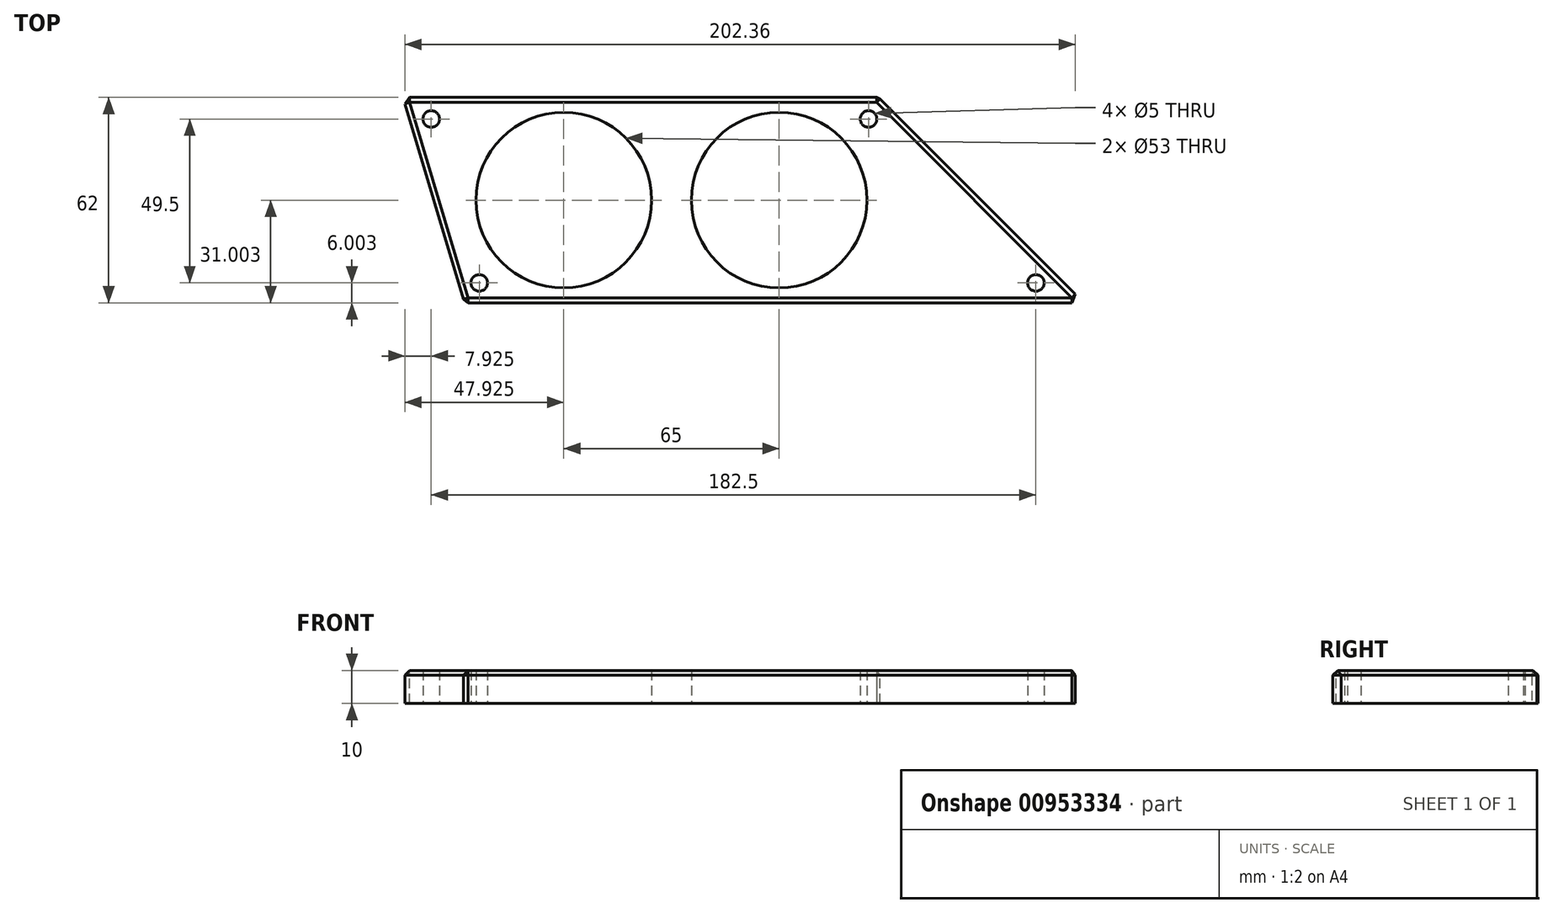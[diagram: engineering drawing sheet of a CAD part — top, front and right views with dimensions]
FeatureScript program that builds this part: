
annotation { "Feature Type Name" : "Feature", "Feature Type Description" : "" }
export const myFeature = defineFeature(function(context is Context, id is Id, definition is map)
    precondition{}
    {
        {
            var Q0;
            Q0=qCreatedBy(makeId("Top.planeOp"),FACE);
            var sketch = newSketch(context, id + "F0", { "sketchPlane" : qUnion([Q0])});
            skLineSegment(sketch, "E0", {"start": v(-45.67, 49.77) * mm, "end": v(97.83, 49.77) * mm});
            skLineSegment(sketch, "E1", {"start": v(97.83, 49.77) * mm, "end": v(159.83, -12.23) * mm});
            skLineSegment(sketch, "E2", {"start": v(159.83, -12.23) * mm, "end": v(-27.17, -12.23) * mm});
            skLineSegment(sketch, "E3", {"start": v(-27.17, -12.23) * mm, "end": v(-45.67, 49.77) * mm});
            skCircle(sketch, "E4", {"center": v(2.83, 18.77) * mm, "radius": 26.5 * mm});
            skCircle(sketch, "E5", {"center": v(67.83, 18.77) * mm, "radius": 26.5 * mm});
            skPoint(sketch, "E6", {"position": v(-37.17, 43.27) * mm});
            skPoint(sketch, "E7", {"position": v(-22.67, -6.23) * mm});
            skPoint(sketch, "E8", {"position": v(94.83, 43.27) * mm});
            skPoint(sketch, "E9", {"position": v(145.33, -6.23) * mm});
            skSolve(sketch);
        }
        {
            var Q0;
            Q0=makeQuery(id+"F0.imprint","IMPRINT",FACE,{"disambiguationData":[TD([[makeQuery(id+"F0.imprint","IMPRINT",EDGE,{"derivedFrom":sQuery(id+"F0.wireOp",EDGE,"E0")}),-1.0]])]});
            extrude(context, id + "F1", {"entities" : qUnion([Q0]), "depth" : 10 * mm, "offsetDistance" : 25 * mm});
        }
        {
            var Q0;
            Q0=sQuery(id+"F0.wireOp",VERTEX,"E6");
            var Q1;
            Q1=sQuery(id+"F0.wireOp",VERTEX,"E7");
            var Q2;
            Q2=sQuery(id+"F0.wireOp",VERTEX,"E8");
            var Q3;
            Q3=sQuery(id+"F0.wireOp",VERTEX,"E9");
            var Q4;
            Q4=makeQuery(id+"F1.opExtrude","SWEPT_BODY",BODY,{"disambiguationData":[OSD([sQuery(id+"F0.wireOp",EDGE,"E0"),sQuery(id+"F0.wireOp",EDGE,"E1"),sQuery(id+"F0.wireOp",EDGE,"E2"),sQuery(id+"F0.wireOp",EDGE,"E3"),sQuery(id+"F0.wireOp",EDGE,"E4"),sQuery(id+"F0.wireOp",EDGE,"E5")])]});
            hole(context, id + "F2", {"style" : HoleStyle.SIMPLE, "endStyle" : HoleEndStyle.BLIND, "oppositeDirection" : true, "holeDiameter" : 5 * mm, "majorDiameter" : 5 * mm, "holeDepth" : 25 * mm, "isTappedThrough" : true, "tappedDepth" : 5 * mm, "tapClearance" : 3, "startFromSketch" : true, "locations" : qUnion([Q0, Q1, Q2, Q3]), "scope" : qUnion([Q4])});
        }
        {
            var Q0;
            Q0=makeQuery(id+"F2.hole-0.boolean.opBoolean","INTERSECT",EDGE,{"derivedFrom":[makeQuery(id+"F1.opExtrude","CAP_FACE",FACE,{"disambiguationData":[OSD([sQuery(id+"F0.wireOp",EDGE,"E0"),sQuery(id+"F0.wireOp",EDGE,"E1"),sQuery(id+"F0.wireOp",EDGE,"E2"),sQuery(id+"F0.wireOp",EDGE,"E3"),sQuery(id+"F0.wireOp",EDGE,"E4"),sQuery(id+"F0.wireOp",EDGE,"E5")])],"isStart":false}),makeQuery(id+"F2.hole-0.opRevolve","SWEPT_FACE",FACE,{"disambiguationData":[OSD([sQuery(id+"F2.hole-0.sketch.wireOp",EDGE,"core_line_2")])]})]});
            var Q1;
            Q1=makeQuery(id+"F2.hole-1.boolean.opBoolean","INTERSECT",EDGE,{"derivedFrom":[makeQuery(id+"F1.opExtrude","CAP_FACE",FACE,{"disambiguationData":[OSD([sQuery(id+"F0.wireOp",EDGE,"E0"),sQuery(id+"F0.wireOp",EDGE,"E1"),sQuery(id+"F0.wireOp",EDGE,"E2"),sQuery(id+"F0.wireOp",EDGE,"E3"),sQuery(id+"F0.wireOp",EDGE,"E4"),sQuery(id+"F0.wireOp",EDGE,"E5")])],"isStart":false}),makeQuery(id+"F2.hole-1.opRevolve","SWEPT_FACE",FACE,{"disambiguationData":[OSD([sQuery(id+"F2.hole-1.sketch.wireOp",EDGE,"core_line_2")])]})]});
            var Q2;
            Q2=makeQuery(id+"F2.hole-2.boolean.opBoolean","INTERSECT",EDGE,{"derivedFrom":[makeQuery(id+"F1.opExtrude","CAP_FACE",FACE,{"disambiguationData":[OSD([sQuery(id+"F0.wireOp",EDGE,"E0"),sQuery(id+"F0.wireOp",EDGE,"E1"),sQuery(id+"F0.wireOp",EDGE,"E2"),sQuery(id+"F0.wireOp",EDGE,"E3"),sQuery(id+"F0.wireOp",EDGE,"E4"),sQuery(id+"F0.wireOp",EDGE,"E5")])],"isStart":false}),makeQuery(id+"F2.hole-2.opRevolve","SWEPT_FACE",FACE,{"disambiguationData":[OSD([sQuery(id+"F2.hole-2.sketch.wireOp",EDGE,"core_line_2")])]})]});
            var Q3;
            Q3=makeQuery(id+"F2.hole-3.boolean.opBoolean","INTERSECT",EDGE,{"derivedFrom":[makeQuery(id+"F1.opExtrude","CAP_FACE",FACE,{"disambiguationData":[OSD([sQuery(id+"F0.wireOp",EDGE,"E0"),sQuery(id+"F0.wireOp",EDGE,"E1"),sQuery(id+"F0.wireOp",EDGE,"E2"),sQuery(id+"F0.wireOp",EDGE,"E3"),sQuery(id+"F0.wireOp",EDGE,"E4"),sQuery(id+"F0.wireOp",EDGE,"E5")])],"isStart":false}),makeQuery(id+"F2.hole-3.opRevolve","SWEPT_FACE",FACE,{"disambiguationData":[OSD([sQuery(id+"F2.hole-3.sketch.wireOp",EDGE,"core_line_2")])]})]});
            var Q4;
            Q4=makeQuery(id+"F1.opExtrude","CAP_EDGE",EDGE,{"disambiguationData":[OSD([sQuery(id+"F0.wireOp",EDGE,"E3")])],"isStart":false});
            var Q5;
            Q5=makeQuery(id+"F1.opExtrude","CAP_EDGE",EDGE,{"disambiguationData":[OSD([sQuery(id+"F0.wireOp",EDGE,"E2")])],"isStart":false});
            var Q6;
            Q6=makeQuery(id+"F1.opExtrude","CAP_EDGE",EDGE,{"disambiguationData":[OSD([sQuery(id+"F0.wireOp",EDGE,"E1")])],"isStart":false});
            var Q7;
            Q7=makeQuery(id+"F1.opExtrude","CAP_EDGE",EDGE,{"disambiguationData":[OSD([sQuery(id+"F0.wireOp",EDGE,"E0")])],"isStart":false});
            var Q8;
            Q8=makeQuery(id+"F1.opExtrude","SWEPT_EDGE",EDGE,{"disambiguationData":[OSD([sQuery(id+"F0.wireOp",EDGE,"E2"),sQuery(id+"F0.wireOp",EDGE,"E3")])]});
            var Q9;
            Q9=makeQuery(id+"F1.opExtrude","SWEPT_EDGE",EDGE,{"disambiguationData":[OSD([sQuery(id+"F0.wireOp",EDGE,"E1"),sQuery(id+"F0.wireOp",EDGE,"E2")])]});
            var Q10;
            Q10=makeQuery(id+"F1.opExtrude","SWEPT_EDGE",EDGE,{"disambiguationData":[OSD([sQuery(id+"F0.wireOp",EDGE,"E0"),sQuery(id+"F0.wireOp",EDGE,"E1")])]});
            var Q11;
            Q11=makeQuery(id+"F1.opExtrude","SWEPT_EDGE",EDGE,{"disambiguationData":[OSD([sQuery(id+"F0.wireOp",EDGE,"E0"),sQuery(id+"F0.wireOp",EDGE,"E3")])]});
            chamfer(context, id + "F3", {"entities" : qUnion([Q0, Q1, Q2, Q3, Q4, Q5, Q6, Q7, Q8, Q9, Q10, Q11]), "width" : 1.5 * mm, "tangentPropagation" : true});
        }
    });
